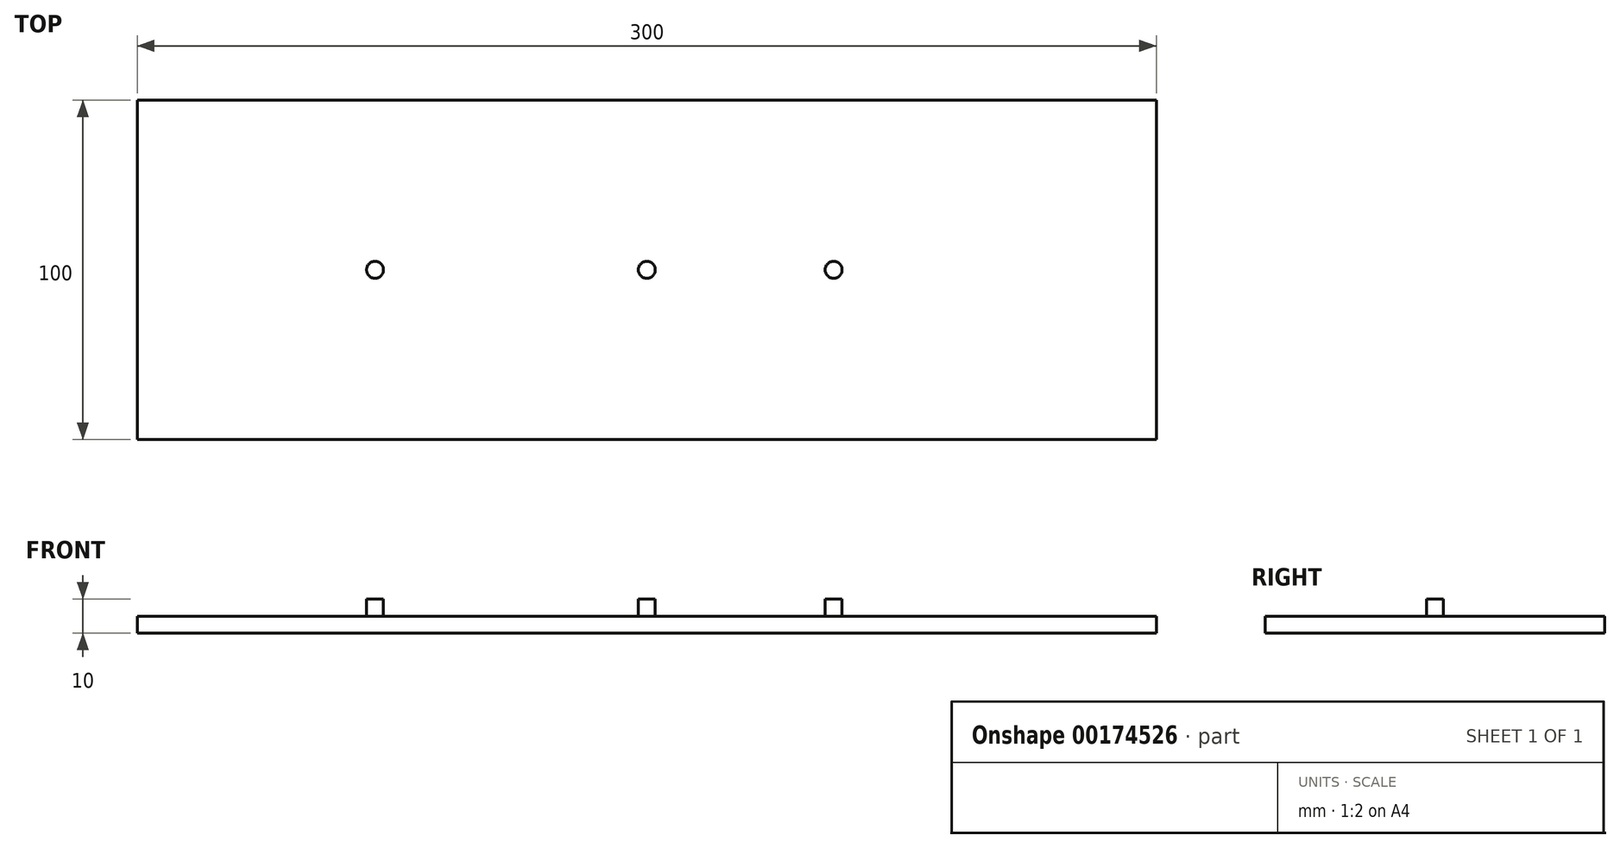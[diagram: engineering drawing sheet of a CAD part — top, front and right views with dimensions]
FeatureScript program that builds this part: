
annotation { "Feature Type Name" : "Feature", "Feature Type Description" : "" }
export const myFeature = defineFeature(function(context is Context, id is Id, definition is map)
    precondition{}
    {
        {
            var Q0;
            Q0=qCreatedBy(makeId("Top.planeOp"),FACE);
            var sketch = newSketch(context, id + "F0", { "sketchPlane" : qUnion([Q0])});
            skLineSegment(sketch, "E0.bottom", {"start": v(-150, 50) * mm, "end": v(150, 50) * mm});
            skLineSegment(sketch, "E0.top", {"start": v(-150, -50) * mm, "end": v(150, -50) * mm});
            skLineSegment(sketch, "E0.left", {"start": v(-150, 50) * mm, "end": v(-150, -50) * mm});
            skLineSegment(sketch, "E0.right", {"start": v(150, 50) * mm, "end": v(150, -50) * mm});
            skSolve(sketch);
        }
        {
            var Q0;
            Q0=makeQuery(id+"F0.imprint","IMPRINT",FACE,{"disambiguationData":[TD([[makeQuery(id+"F0.imprint","IMPRINT",EDGE,{"derivedFrom":sQuery(id+"F0.wireOp",EDGE,"E0.bottom")}),-1.0]])]});
            extrude(context, id + "F1", {"entities" : qUnion([Q0]), "depth" : 5 * mm});
        }
        {
            var Q0;
            Q0=makeQuery(id+"F1.opExtrude","CAP_FACE",FACE,{"disambiguationData":[OSD([sQuery(id+"F0.wireOp",EDGE,"E0.bottom"),sQuery(id+"F0.wireOp",EDGE,"E0.top"),sQuery(id+"F0.wireOp",EDGE,"E0.left"),sQuery(id+"F0.wireOp",EDGE,"E0.right")])],"isStart":false});
            var sketch = newSketch(context, id + "F2", { "sketchPlane" : qUnion([Q0])});
            skCircle(sketch, "E1", {"center": v(0, 0) * mm, "radius": 2.5 * mm});
            skCircle(sketch, "E2", {"center": v(-80, 0) * mm, "radius": 2.5 * mm});
            skCircle(sketch, "E3", {"center": v(55, 0) * mm, "radius": 2.5 * mm});
            skSolve(sketch);
        }
        {
            var Q0;
            Q0=makeQuery(id+"F2.imprint","IMPRINT",FACE,{"disambiguationData":[TD([[makeQuery(id+"F2.imprint","IMPRINT",EDGE,{"derivedFrom":sQuery(id+"F2.wireOp",EDGE,"E1")}),1.0]])]});
            var Q1;
            Q1=makeQuery(id+"F2.imprint","IMPRINT",FACE,{"disambiguationData":[TD([[makeQuery(id+"F2.imprint","IMPRINT",EDGE,{"derivedFrom":sQuery(id+"F2.wireOp",EDGE,"E2")}),1.0]])]});
            extrude(context, id + "F3", {"entities" : qUnion([Q0, Q1]), "operationType" : NewBodyOperationType.ADD, "depth" : 5 * mm});
        }
        {
            var Q0;
            Q0 = qSketchRegion(id + "F2", true);
            extrude(context, id + "F4", {"entities" : qUnion([Q0]), "operationType" : NewBodyOperationType.ADD, "depth" : 5 * mm});
        }
    });
